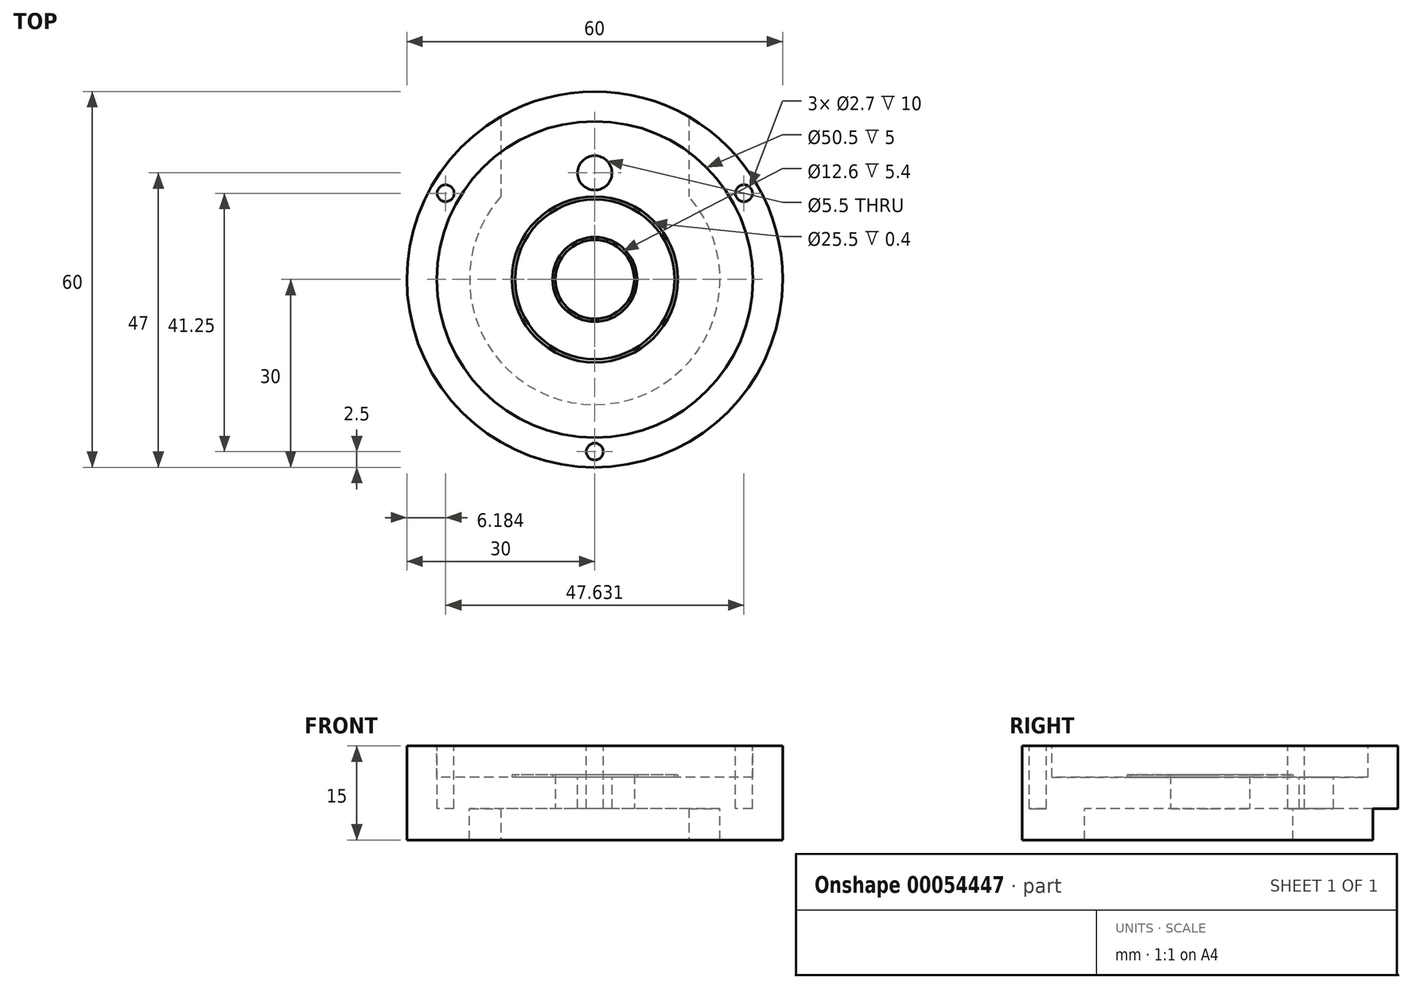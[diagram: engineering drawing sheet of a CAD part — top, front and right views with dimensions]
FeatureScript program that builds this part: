
annotation { "Feature Type Name" : "Feature", "Feature Type Description" : "" }
export const myFeature = defineFeature(function(context is Context, id is Id, definition is map)
    precondition{}
    {
        {
            var Q0;
            Q0=qCreatedBy(makeId("Top.planeOp"),FACE);
            var sketch = newSketch(context, id + "F0", { "sketchPlane" : qUnion([Q0])});
            skCircle(sketch, "E0", {"center": v(0, 0) * mm, "radius": 30 * mm});
            skSolve(sketch);
        }
        {
            var Q0;
            Q0=makeQuery(id+"F0.imprint","IMPRINT",FACE,{"disambiguationData":[TD([[makeQuery(id+"F0.imprint","IMPRINT",EDGE,{"derivedFrom":sQuery(id+"F0.wireOp",EDGE,"E0")}),1.0]])]});
            extrude(context, id + "F1", {"entities" : qUnion([Q0]), "depth" : 10 * mm});
        }
        {
            var Q0;
            Q0=makeQuery(id+"F1.opExtrude","CAP_FACE",FACE,{"disambiguationData":[OSD([sQuery(id+"F0.wireOp",EDGE,"E0")])],"isStart":false});
            var sketch = newSketch(context, id + "F2", { "sketchPlane" : qUnion([Q0])});
            skCircle(sketch, "E1", {"center": v(0, 0) * mm, "radius": 25.25 * mm});
            skSolve(sketch);
        }
        {
            var Q0;
            Q0=makeQuery(id+"F2.imprint","IMPRINT",FACE,{"disambiguationData":[TD([[makeQuery(id+"F2.imprint","IMPRINT",EDGE,{"derivedFrom":sQuery(id+"F2.wireOp",EDGE,"E1")}),1.0]])]});
            extrude(context, id + "F3", {"entities" : qUnion([Q0]), "operationType" : NewBodyOperationType.REMOVE, "oppositeDirection" : true, "depth" : 5 * mm});
        }
        {
            var Q0;
            Q0=qCreatedBy(makeId("Top.planeOp"),FACE);
            var sketch = newSketch(context, id + "F4", { "sketchPlane" : qUnion([Q0])});
            skCircle(sketch, "E2", {"center": v(0, 0) * mm, "radius": 6.3 * mm});
            skSolve(sketch);
        }
        {
            var Q0;
            Q0=makeQuery(id+"F4.imprint","IMPRINT",FACE,{"disambiguationData":[TD([[makeQuery(id+"F4.imprint","IMPRINT",EDGE,{"derivedFrom":sQuery(id+"F4.wireOp",EDGE,"E2")}),1.0]])]});
            var Q1;
            Q1=sQuery(id+"F4.wireOp",EDGE,"E2");
            extrude(context, id + "F5", {"entities" : qUnion([Q0]), "operationType" : NewBodyOperationType.REMOVE, "surfaceEntities" : qUnion([Q1]), "endBound" : BoundingType.THROUGH_ALL, "depth" : 25 * mm});
        }
        {
            var Q0;
            Q0=makeQuery(id+"F1.opExtrude","CAP_FACE",FACE,{"disambiguationData":[OSD([sQuery(id+"F0.wireOp",EDGE,"E0")])],"isStart":false});
            var sketch = newSketch(context, id + "F6", { "sketchPlane" : qUnion([Q0])});
            skLineSegment(sketch, "E3", {"start": v(0, 0) * mm, "end": v(25.25, 0) * mm, "construction": true});
            skCircle(sketch, "E4", {"center": v(23.82, 13.75) * mm, "radius": 1.35 * mm});
            skCircle(sketch, "E5", {"center": v(0, -27.5) * mm, "radius": 1.35 * mm});
            skLineSegment(sketch, "E6", {"start": v(0, 0) * mm, "end": v(23.82, 13.75) * mm, "construction": true});
            skLineSegment(sketch, "E7", {"start": v(0, 0) * mm, "end": v(0, -27.5) * mm, "construction": true});
            skLineSegment(sketch, "E8", {"start": v(0, 0) * mm, "end": v(-23.82, 13.75) * mm, "construction": true});
            skCircle(sketch, "E9", {"center": v(-23.82, 13.75) * mm, "radius": 1.35 * mm});
            skSolve(sketch);
        }
        {
            var Q0;
            Q0=makeQuery(id+"F6.imprint","IMPRINT",FACE,{"disambiguationData":[TD([[makeQuery(id+"F6.imprint","IMPRINT",EDGE,{"derivedFrom":sQuery(id+"F6.wireOp",EDGE,"E4")}),1.0]])]});
            var Q1;
            Q1=makeQuery(id+"F6.imprint","IMPRINT",FACE,{"disambiguationData":[TD([[makeQuery(id+"F6.imprint","IMPRINT",EDGE,{"derivedFrom":sQuery(id+"F6.wireOp",EDGE,"E5")}),1.0]])]});
            var Q2;
            Q2=makeQuery(id+"F6.imprint","IMPRINT",FACE,{"disambiguationData":[TD([[makeQuery(id+"F6.imprint","IMPRINT",EDGE,{"derivedFrom":sQuery(id+"F6.wireOp",EDGE,"E9")}),1.0]])]});
            var Q3;
            Q3=sQuery(id+"F6.wireOp",EDGE,"ec20421c-758a-4dcc-8e2b-3ec363aacf1b");
            var Q4;
            Q4=sQuery(id+"F6.wireOp",EDGE,"3d322e7b-1bf5-4eee-8f98-b2096053c3f1");
            extrude(context, id + "F7", {"entities" : qUnion([Q0, Q1, Q2]), "operationType" : NewBodyOperationType.REMOVE, "surfaceEntities" : qUnion([Q3, Q4]), "endBound" : BoundingType.THROUGH_ALL, "oppositeDirection" : true, "depth" : 25 * mm});
        }
        {
            var Q0;
            Q0=makeQuery(id+"F3.boolean.opBoolean","COPY",FACE,{"derivedFrom":makeQuery(id+"F3.opExtrude","CAP_FACE",FACE,{"disambiguationData":[OSD([sQuery(id+"F2.wireOp",EDGE,"E1")])],"isStart":false})});
            var sketch = newSketch(context, id + "F8", { "sketchPlane" : qUnion([Q0])});
            skLineSegment(sketch, "E10", {"start": v(0, 0) * mm, "end": v(0, 17) * mm, "construction": true});
            skCircle(sketch, "E11", {"center": v(0, 17) * mm, "radius": 2.75 * mm});
            skSolve(sketch);
        }
        {
            var Q0;
            Q0=makeQuery(id+"F8.imprint","IMPRINT",FACE,{"disambiguationData":[TD([[makeQuery(id+"F8.imprint","IMPRINT",EDGE,{"derivedFrom":sQuery(id+"F8.wireOp",EDGE,"E11")}),1.0]])]});
            var Q1;
            Q1=sQuery(id+"F8.wireOp",EDGE,"E11");
            extrude(context, id + "F9", {"entities" : qUnion([Q0]), "operationType" : NewBodyOperationType.REMOVE, "surfaceEntities" : qUnion([Q1]), "endBound" : BoundingType.THROUGH_ALL, "oppositeDirection" : true, "depth" : 25 * mm});
        }
        {
            var Q0;
            Q0=makeQuery(id+"F1.opExtrude","CAP_FACE",FACE,{"disambiguationData":[OSD([sQuery(id+"F0.wireOp",EDGE,"E0")])],"isStart":true});
            var sketch = newSketch(context, id + "F10", { "sketchPlane" : qUnion([Q0])});
            skCircle(sketch, "E12", {"center": v(0, 0) * mm, "radius": 30 * mm});
            skCircle(sketch, "E13", {"center": v(0, 0) * mm, "radius": 20 * mm});
            skSolve(sketch);
        }
        {
            var Q0;
            Q0=qSketchRegion(id+"F10",true);
            extrude(context, id + "F11", {"entities" : qUnion([Q0]), "operationType" : NewBodyOperationType.ADD, "depth" : 5 * mm});
        }
        {
            var Q0;
            Q0=qCreatedBy(makeId("Top.planeOp"),FACE);
            var sketch = newSketch(context, id + "F12", { "sketchPlane" : qUnion([Q0])});
            skLineSegment(sketch, "E14.rect.bottom", {"start": v(-15, 33.3) * mm, "end": v(15, 33.3) * mm});
            skLineSegment(sketch, "E14.rect.top", {"start": v(-15, 8.53) * mm, "end": v(15, 8.53) * mm});
            skLineSegment(sketch, "E14.rect.left", {"start": v(-15, 33.3) * mm, "end": v(-15, 8.53) * mm});
            skLineSegment(sketch, "E14.rect.right", {"start": v(15, 33.3) * mm, "end": v(15, 8.53) * mm});
            skPoint(sketch, "E14.rect.middle", {"position": v(0, 20.91) * mm});
            skSolve(sketch);
        }
        {
            var Q0;
            Q0=makeQuery(id+"F12.imprint","IMPRINT",FACE,{"disambiguationData":[TD([[makeQuery(id+"F12.imprint","IMPRINT",EDGE,{"derivedFrom":sQuery(id+"F12.wireOp",EDGE,"E14.rect.bottom")}),-1.0]])]});
            extrude(context, id + "F13", {"entities" : qUnion([Q0]), "operationType" : NewBodyOperationType.REMOVE, "oppositeDirection" : true, "depth" : 5 * mm});
        }
        {
            var Q0;
            Q0=makeQuery(id+"F3.boolean.opBoolean","COPY",FACE,{"derivedFrom":makeQuery(id+"F3.opExtrude","CAP_FACE",FACE,{"disambiguationData":[OSD([sQuery(id+"F2.wireOp",EDGE,"E1")])],"isStart":false})});
            var sketch = newSketch(context, id + "F14", { "sketchPlane" : qUnion([Q0])});
            skCircle(sketch, "E15", {"center": v(0, 0) * mm, "radius": 6.25 * mm});
            skCircle(sketch, "E16", {"center": v(0, 0) * mm, "radius": 6.75 * mm});
            skCircle(sketch, "E17", {"center": v(0, 0) * mm, "radius": 12.75 * mm});
            skCircle(sketch, "E18", {"center": v(0, 0) * mm, "radius": 13.25 * mm});
            skSolve(sketch);
        }
        {
            var Q0;
            Q0 = qSketchRegion(id + "F14", true);
            var Q1;
            Q1=makeQuery(id+"F14.imprint","IMPRINT",FACE,{"disambiguationData":[TD([[makeQuery(id+"F14.imprint","IMPRINT",EDGE,{"derivedFrom":sQuery(id+"F14.wireOp",EDGE,"E16")}),1.0]])]});
            extrude(context, id + "F15", {"entities" : qUnion([Q0, Q1]), "operationType" : NewBodyOperationType.ADD, "depth" : .4 * mm});
        }
    });
